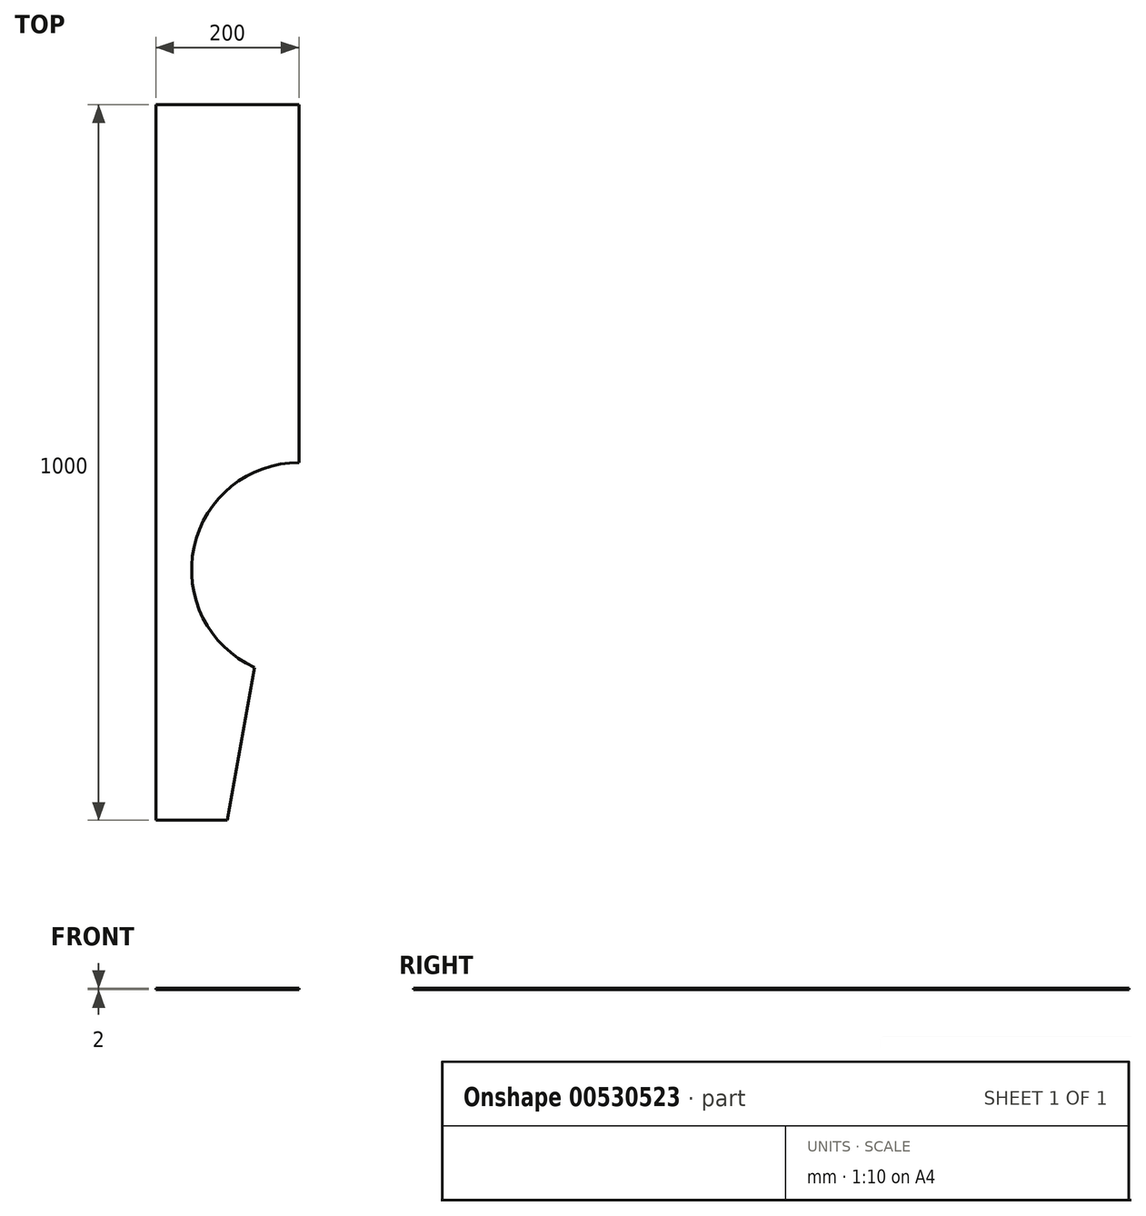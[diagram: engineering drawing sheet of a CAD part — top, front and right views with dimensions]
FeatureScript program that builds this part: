
annotation { "Feature Type Name" : "Feature", "Feature Type Description" : "" }
export const myFeature = defineFeature(function(context is Context, id is Id, definition is map)
    precondition{}
    {
        {
            var Q0;
            Q0=qCreatedBy(makeId("Top.planeOp"),FACE);
            var sketch = newSketch(context, id + "F0", { "sketchPlane" : qUnion([Q0])});
            skLineSegment(sketch, "E0.bottom", {"start": v(-100, 0) * mm, "end": v(-200, 0) * mm});
            skLineSegment(sketch, "E0.top", {"start": v(0, 1000) * mm, "end": v(-200, 1000) * mm});
            skLineSegment(sketch, "E0.left", {"start": v(0, 500) * mm, "end": v(0, 1000) * mm});
            skLineSegment(sketch, "E0.right", {"start": v(-200, 0) * mm, "end": v(-200, 1000) * mm});
            skLineSegment(sketch, "E1", {"start": v(-100, 0) * mm, "end": v(-62.34, 213.57) * mm});
            skArc(sketch, "E2", {"start": v(0, 500) * mm, "mid": v(-146.57, 381.9) * mm, "end": v(-62.34, 213.57) * mm});
            skPoint(sketch, "E3.orphan", {"position": v(0, 0) * mm});
            skSolve(sketch);
        }
        {
            var Q0;
            Q0=makeQuery(id+"F0.imprint","IMPRINT",FACE,{"disambiguationData":[TD([[makeQuery(id+"F0.imprint","IMPRINT",EDGE,{"derivedFrom":sQuery(id+"F0.wireOp",EDGE,"E0.bottom")}),-1.0]])]});
            extrude(context, id + "F1", {"entities" : qUnion([Q0]), "depth" : 2 * mm, "offsetDistance" : 25 * mm});
        }
    });
